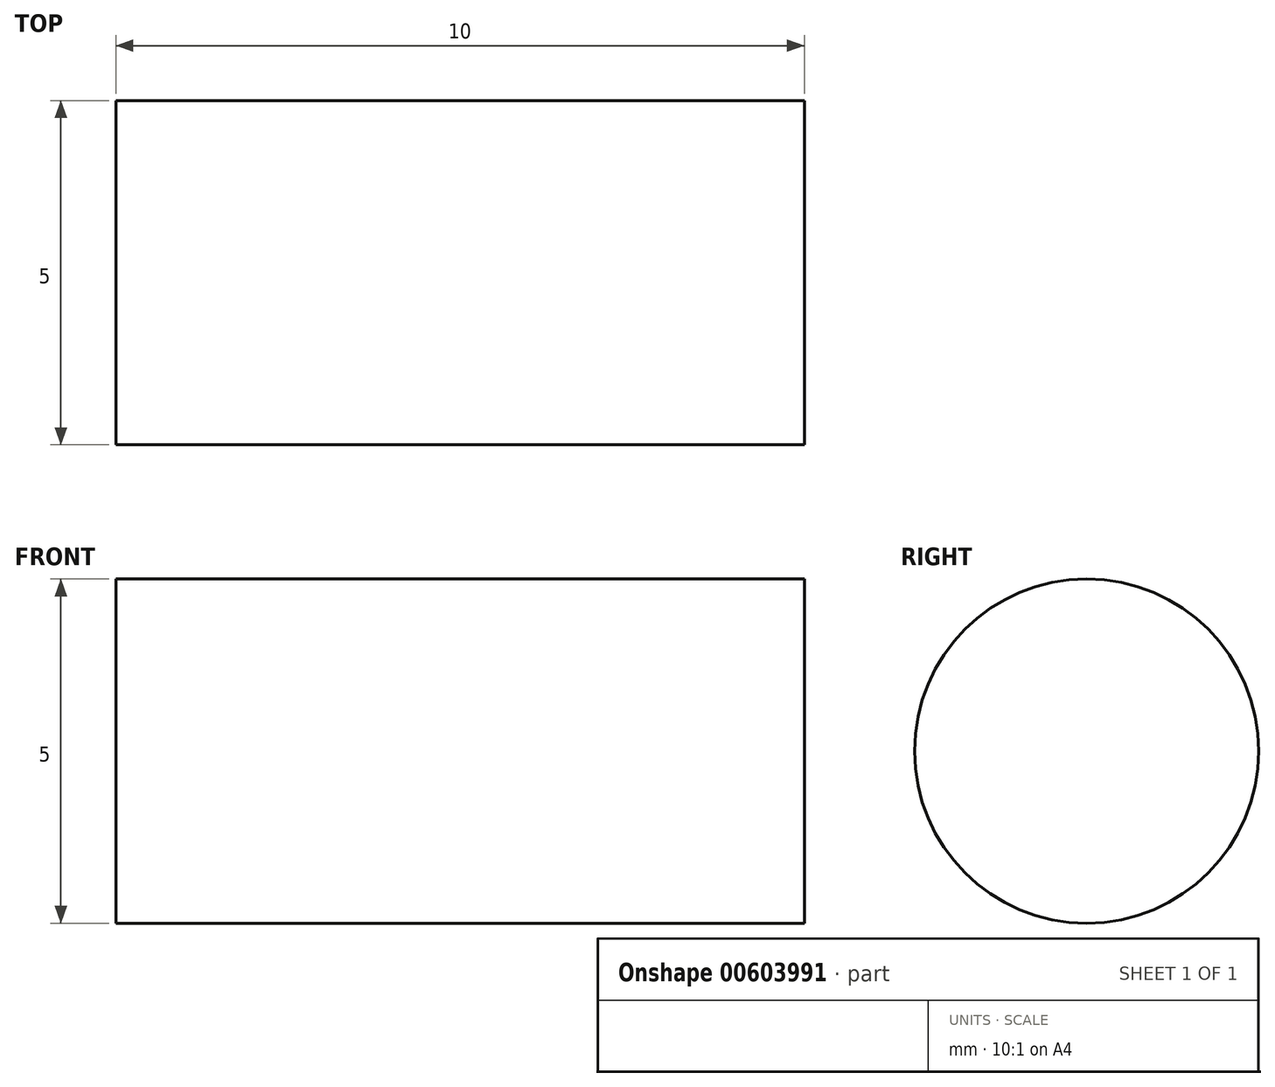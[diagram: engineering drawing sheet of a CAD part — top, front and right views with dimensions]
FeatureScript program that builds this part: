
annotation { "Feature Type Name" : "Feature", "Feature Type Description" : "" }
export const myFeature = defineFeature(function(context is Context, id is Id, definition is map)
    precondition{}
    {
        {
            var Q0;
            Q0=qCreatedBy(makeId("Front.planeOp"),FACE);
            var sketch = newSketch(context, id + "F0", { "sketchPlane" : qUnion([Q0])});
            skLineSegment(sketch, "E0", {"start": v(0, 0) * mm, "end": v(0, 3.5) * mm});
            skLineSegment(sketch, "E1", {"start": v(0, 3.5) * mm, "end": v(-4, 5) * mm});
            skLineSegment(sketch, "E2", {"start": v(-4, 5) * mm, "end": v(-10, 5) * mm});
            skArc(sketch, "E3", {"start": v(-20, 15) * mm, "mid": v(-17.07, 7.93) * mm, "end": v(-10, 5) * mm});
            skLineSegment(sketch, "E4.bottom", {"start": v(-20, 15) * mm, "end": v(-27, 15) * mm});
            skLineSegment(sketch, "E4.top", {"start": v(-20, 0) * mm, "end": v(-27, 0) * mm});
            skLineSegment(sketch, "E5.bottom", {"start": v(-27, 13) * mm, "end": v(-30, 13) * mm});
            skLineSegment(sketch, "E5.top", {"start": v(-27, 0) * mm, "end": v(-30, 0) * mm});
            skLineSegment(sketch, "E6.bottom", {"start": v(-35, 15) * mm, "end": v(-30, 15) * mm});
            skLineSegment(sketch, "E6.top", {"start": v(-35, 0) * mm, "end": v(-30, 0) * mm});
            skLineSegment(sketch, "E7.bottom", {"start": v(-35, 13) * mm, "end": v(-37, 13) * mm});
            skLineSegment(sketch, "E7.top", {"start": v(-35, 0) * mm, "end": v(-37, 0) * mm});
            skLineSegment(sketch, "E8.bottom", {"start": v(-40, 15) * mm, "end": v(-37, 15) * mm});
            skLineSegment(sketch, "E8.top", {"start": v(-40, 0) * mm, "end": v(-37, 0) * mm});
            skLineSegment(sketch, "E9.bottom", {"start": v(-50, 20) * mm, "end": v(-40, 20) * mm});
            skLineSegment(sketch, "E9.top", {"start": v(-50, 0) * mm, "end": v(-40, 0) * mm});
            skLineSegment(sketch, "E9.left", {"start": v(-50, 20) * mm, "end": v(-50, 0) * mm});
            skLineSegment(sketch, "E10", {"start": v(-27, 15) * mm, "end": v(-27, 13) * mm});
            skLineSegment(sketch, "E11", {"start": v(-30, 15) * mm, "end": v(-30, 13) * mm});
            skLineSegment(sketch, "E12", {"start": v(-35, 15) * mm, "end": v(-35, 13) * mm});
            skLineSegment(sketch, "E13", {"start": v(-37, 15) * mm, "end": v(-37, 13) * mm});
            skLineSegment(sketch, "E14", {"start": v(-40, 20) * mm, "end": v(-40, 15) * mm});
            skLineSegment(sketch, "E15", {"start": v(-50, 0) * mm, "end": v(0, 0) * mm});
            skLineSegment(sketch, "E16.bottom", {"start": v(0, 2.5) * mm, "end": v(-10, 2.5) * mm});
            skLineSegment(sketch, "E16.top", {"start": v(0, 0) * mm, "end": v(-10, 0) * mm});
            skLineSegment(sketch, "E16.left", {"start": v(0, 2.5) * mm, "end": v(0, 0) * mm});
            skLineSegment(sketch, "E16.right", {"start": v(-10, 2.5) * mm, "end": v(-10, 0) * mm});
            skLineSegment(sketch, "E17", {"start": v(-10, 2.5) * mm, "end": v(-12, 2) * mm});
            skLineSegment(sketch, "E18", {"start": v(-12, 2) * mm, "end": v(-12, 0) * mm});
            skLineSegment(sketch, "E19", {"start": v(-12, 0) * mm, "end": v(-10, 0) * mm});
            skSolve(sketch);
        }
        {
            var Q0;
            Q0=makeQuery(id+"F0.imprint","IMPRINT",FACE,{"disambiguationData":[TD([[makeQuery(id+"F0.imprint","IMPRINT",EDGE,{"derivedFrom":sQuery(id+"F0.wireOp",EDGE,"E0")}),1.0]])]});
            var Q1;
            Q1=sQuery(id+"F0.wireOp",EDGE,"E15");
            revolve(context, id + "F1", {"entities" : qUnion([Q0]), "axis" : qUnion([Q1]), "revolveType" : RevolveType.FULL});
        }
    });
